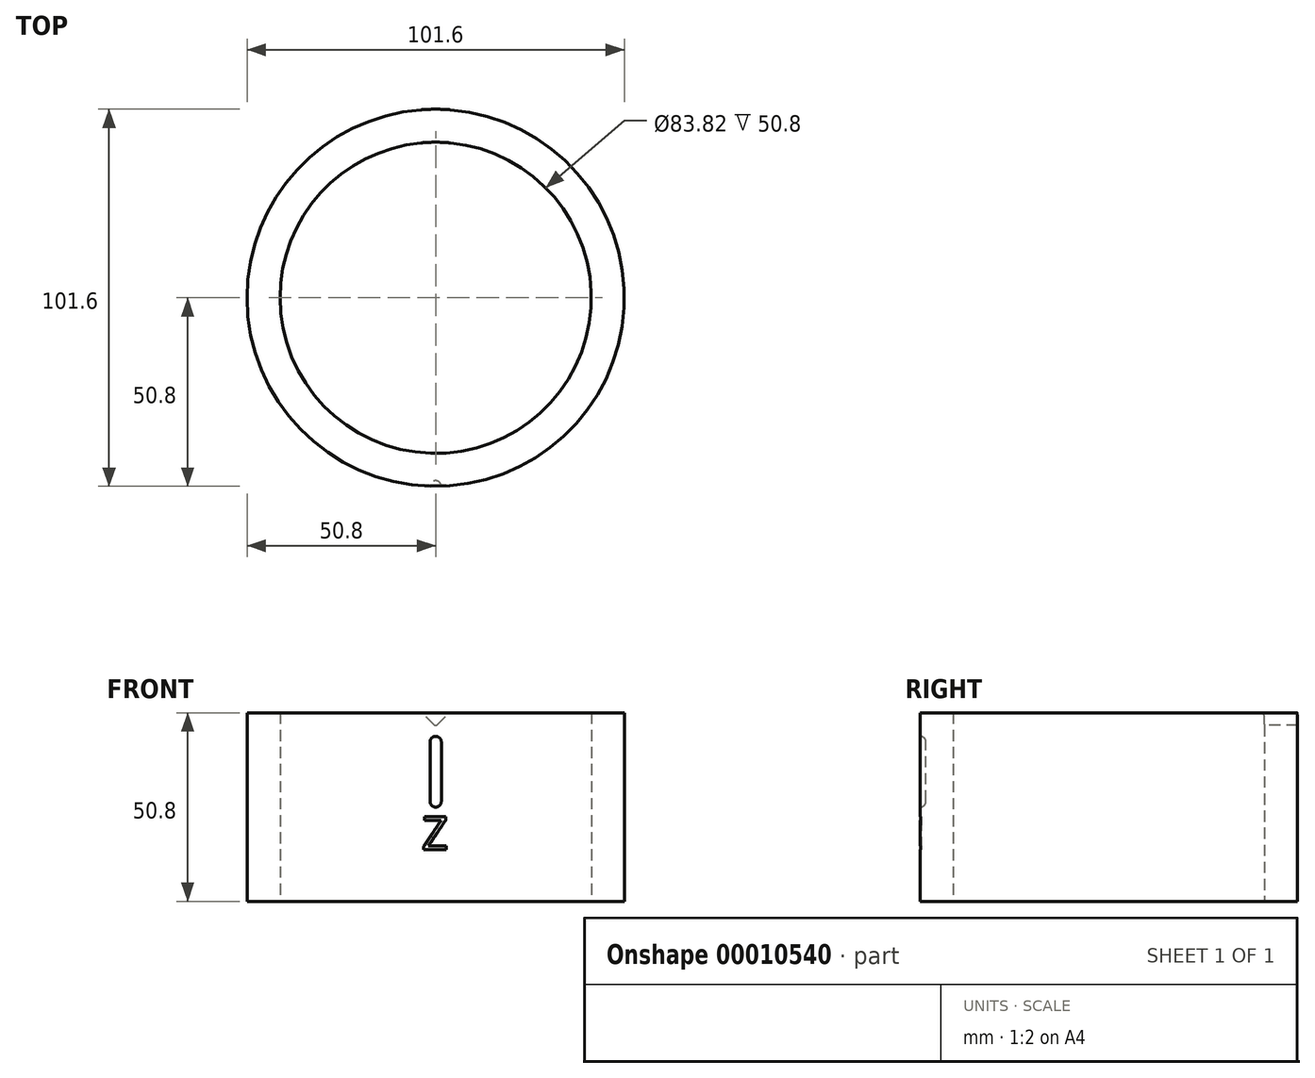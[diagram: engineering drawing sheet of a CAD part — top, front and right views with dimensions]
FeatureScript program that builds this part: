
annotation { "Feature Type Name" : "Feature", "Feature Type Description" : "" }
export const myFeature = defineFeature(function(context is Context, id is Id, definition is map)
    precondition{}
    {
        {
            var Q0;
            Q0=qCreatedBy(makeId("Front.planeOp"),FACE);
            var sketch = newSketch(context, id + "F0", { "sketchPlane" : qUnion([Q0])});
            skLineSegment(sketch, "E0", {"start": v(0, 0) * mm, "end": v(0, 73.3) * mm, "construction": true});
            skLineSegment(sketch, "E1", {"start": v(0, 0) * mm, "end": v(106.58, 0) * mm, "construction": true});
            skLineSegment(sketch, "E2.bottom", {"start": v(41.91, 50.8) * mm, "end": v(50.8, 50.8) * mm});
            skLineSegment(sketch, "E2.top", {"start": v(41.91, 0) * mm, "end": v(50.8, 0) * mm});
            skLineSegment(sketch, "E2.left", {"start": v(41.91, 50.8) * mm, "end": v(41.91, 0) * mm});
            skLineSegment(sketch, "E2.right", {"start": v(50.8, 50.8) * mm, "end": v(50.8, 0) * mm});
            skSolve(sketch);
        }
        {
            var Q0;
            Q0 = qSketchRegion(id + "F0", true);
            var Q1;
            Q1=sQuery(id+"F0.wireOp",EDGE,"E0");
            revolve(context, id + "F1", {"entities" : qUnion([Q0]), "axis" : qUnion([Q1]), "revolveType" : RevolveType.FULL});
        }
        {
            var Q0;
            Q0=qCreatedBy(makeId("Right.planeOp"),FACE);
            var sketch = newSketch(context, id + "F2", { "sketchPlane" : qUnion([Q0])});
            skLineSegment(sketch, "E3.right", {"start": v(-49.28, 42.93) * mm, "end": v(-49.28, 26.92) * mm});
            skArc(sketch, "E4.filletArc", {"start": v(-49.28, 42.93) * mm, "mid": v(-49.72, 44) * mm, "end": v(-50.8, 44.45) * mm});
            skArc(sketch, "E5.filletArc", {"start": v(-50.8, 25.4) * mm, "mid": v(-49.72, 25.85) * mm, "end": v(-49.28, 26.92) * mm});
            skLineSegment(sketch, "E6", {"start": v(-50.8, 44.45) * mm, "end": v(-50.8, 25.4) * mm, "construction": true});
            skLineSegment(sketch, "E7", {"start": v(-50.8, 0) * mm, "end": v(-50.8, 50.8) * mm});
            skLineSegment(sketch, "E8", {"start": v(-50.8, 0) * mm, "end": v(-50.8, 50.8) * mm, "construction": true});
            skSolve(sketch);
        }
        {
            var Q0;
            Q0 = qSketchRegion(id + "F2", true);
            var Q1;
            Q1=sQuery(id+"F2.wireOp",EDGE,"E7");
            revolve(context, id + "F3", {"operationType" : NewBodyOperationType.REMOVE, "entities" : qUnion([Q0]), "axis" : qUnion([Q1]), "revolveType" : RevolveType.FULL, "oppositeDirection" : true});
        }
        {
            var Q0;
            Q0=qCreatedBy(makeId("Front.planeOp"),FACE);
            cPlane(context, id + "F4", {"entities" : qUnion([Q0]), "cplaneType" : CPlaneType.OFFSET, "offset" : 3.3 * mm, "oppositeDirection" : true, "width" : 152.4 * mm, "height" : 152.4 * mm});
        }
        {
            var Q0;
            Q0=qCreatedBy(makeId("Right.planeOp"),FACE);
            var sketch = newSketch(context, id + "F5", { "sketchPlane" : qUnion([Q0])});
            skLineSegment(sketch, "E9", {"start": v(3.3, 50.8) * mm, "end": v(3.3, 0) * mm, "construction": true});
            skSolve(sketch);
        }
        {
            var Q0;
            Q0=qCreatedBy(id+"F4.planeOp",FACE);
            var sketch = newSketch(context, id + "F6", { "sketchPlane" : qUnion([Q0])});
            skLineSegment(sketch, "E10", {"start": v(0, 0) * mm, "end": v(0, 50.8) * mm, "construction": true});
            skLineSegment(sketch, "E11", {"start": v(-3.99, 50.8) * mm, "end": v(0, 50.8) * mm});
            skLineSegment(sketch, "E12.MirrorCS", {"start": v(3.99, 50.8) * mm, "end": v(0, 50.8) * mm});
            skLineSegment(sketch, "E13.MirrorCS", {"start": v(-0.54, 47.66) * mm, "end": v(-3.45, 50.58) * mm});
            skArc(sketch, "E14", {"start": v(-0.54, 47.66) * mm, "mid": v(-0.3, 47.5) * mm, "end": v(0, 47.44) * mm});
            skArc(sketch, "E15", {"start": v(-3.45, 50.58) * mm, "mid": v(-3.7, 50.74) * mm, "end": v(-3.99, 50.8) * mm});
            skPoint(sketch, "E16.orphan", {"position": v(0, 47.13) * mm});
            skLineSegment(sketch, "E17", {"start": v(0, 48.2) * mm, "end": v(0, 47.13) * mm, "construction": true});
            skArc(sketch, "E18.MirrorCS", {"start": v(0.54, 47.66) * mm, "mid": v(0.3, 47.5) * mm, "end": v(0, 47.44) * mm});
            skLineSegment(sketch, "E19.MirrorCS", {"start": v(0.54, 47.66) * mm, "end": v(3.45, 50.58) * mm});
            skArc(sketch, "E20.MirrorCS", {"start": v(3.45, 50.58) * mm, "mid": v(3.7, 50.74) * mm, "end": v(3.99, 50.8) * mm});
            skSolve(sketch);
        }
        {
            var Q0;
            Q0 = qSketchRegion(id + "F6", true);
            extrude(context, id + "F7", {"entities" : qUnion([Q0]), "operationType" : NewBodyOperationType.REMOVE, "endBound" : BoundingType.THROUGH_ALL, "oppositeDirection" : true, "depth" : 25.4 * mm});
        }
        {
            var Q0;
            Q0=makeQuery(id+"F3.boolean.opBoolean","INTERSECT",EDGE,{"derivedFrom":[makeQuery(id+"F1.opRevolve","SWEPT_FACE",FACE,{"disambiguationData":[OSD([sQuery(id+"F0.wireOp",EDGE,"E2.right")])]}),makeQuery(id+"F3.opRevolve","SWEPT_FACE",FACE,{"disambiguationData":[OSD([sQuery(id+"F2.wireOp",EDGE,"E5.filletArc")])]})]});
            cPoint(context, id + "F8", {"entities" : qUnion([Q0]), "parameter" : 0.5});
        }
        {
            var Q0;
            Q0 = qCreatedBy(id + "F8" ,VERTEX);
            var Q1;
            Q1=qCreatedBy(makeId("Front.planeOp"),FACE);
            cPlane(context, id + "F9", {"entities" : qUnion([Q0, Q1]), "cplaneType" : CPlaneType.PLANE_POINT, "offset" : 25.4 * mm, "width" : 152.4 * mm, "height" : 152.4 * mm});
        }
        {
            var Q0;
            Q0=qCreatedBy(id+"F9.planeOp",FACE);
            var sketch = newSketch(context, id + "F10", { "sketchPlane" : qUnion([Q0])});
            skText(sketch, "E21", { "text": "Z", "fontName": "OpenSans-Regular.ttf"});
            const initialGuessF10  = {"E21": [-0.00368, 0.01397, 1, 0, 0.00889]};
            skSetInitialGuess(sketch, initialGuessF10);
            skSolve(sketch);
        }
        {
            var Q0;
            Q0 = qSketchRegion(id + "F10", true);
            extrude(context, id + "F11", {"entities" : qUnion([Q0]), "operationType" : NewBodyOperationType.REMOVE, "oppositeDirection" : true, "depth" : 0.25 * mm});
        }
    });
